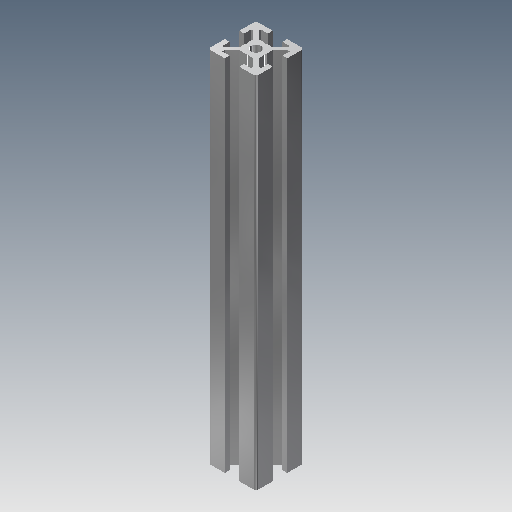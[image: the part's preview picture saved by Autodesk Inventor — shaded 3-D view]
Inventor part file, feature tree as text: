
AUTODESK INVENTOR PART (.ipt)
format: ipt  version: 2017 (Build 210142000, 142)  size: 167,936 bytes
history: native  units: mm
features: extrude x1, sketch x1
ambient origin geometry x8: Origin, YZ Plane, XZ Plane, XY Plane, X Axis, Y Axis, Z Axis, Center Point
bodies: Solid1 (feature_tree)
feature tree (2):
  extrude  "Extrusion1"  [1 undecoded]
  sketch  "Sketch1"  dims[d0=150.0mm d1=0.0mm]
note: 1 required parameter value undecoded (feature->parameter linkage not recoverable at this tier; creation-order binding heuristic only, values carry confidence <= 0.55)
